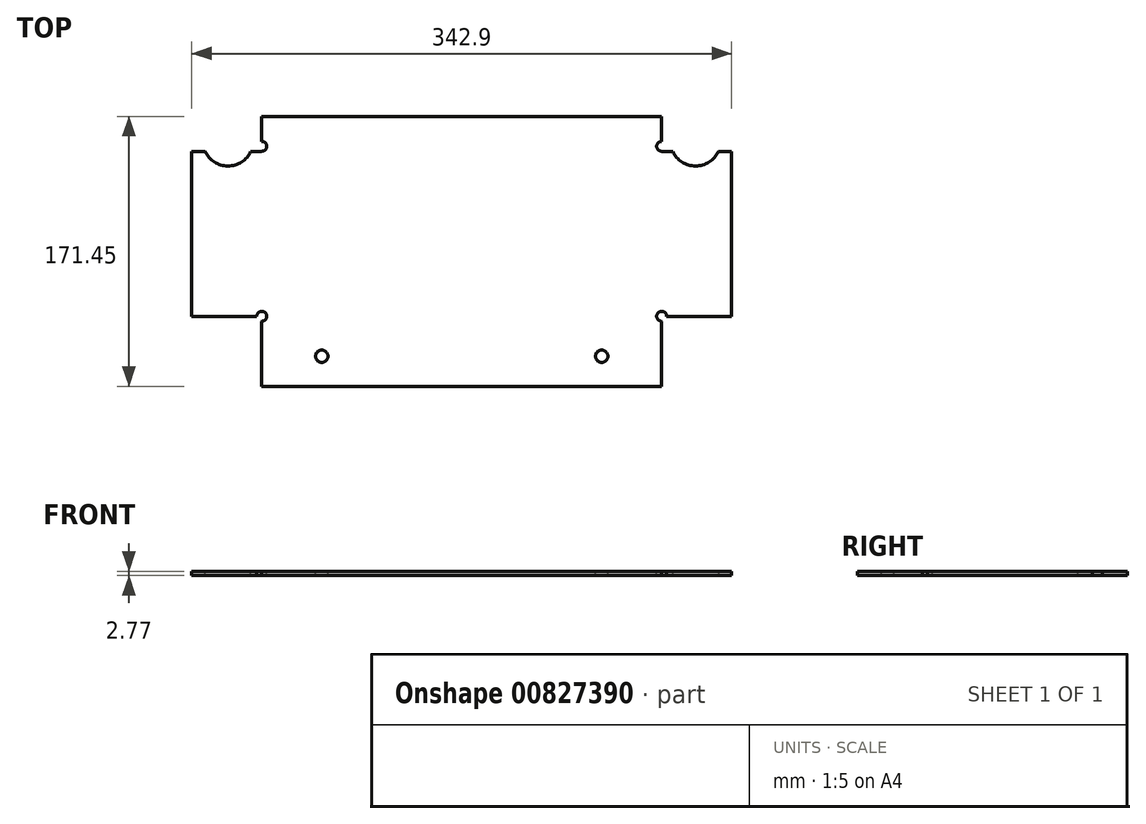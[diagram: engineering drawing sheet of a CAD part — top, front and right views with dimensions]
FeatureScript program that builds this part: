
annotation { "Feature Type Name" : "Feature", "Feature Type Description" : "" }
export const myFeature = defineFeature(function(context is Context, id is Id, definition is map)
    precondition{}
    {
        {
            var Q0;
            Q0=qCreatedBy(makeId("Top.planeOp"),FACE);
            var sketch = newSketch(context, id + "F0", { "sketchPlane" : qUnion([Q0])});
            skArc(sketch, "E0", {"start": v(-162.97, 39.69) * mm, "mid": v(-148.5, 30.35) * mm, "end": v(-134.04, 39.69) * mm});
            skLineSegment(sketch, "E1", {"start": v(-127, 61.91) * mm, "end": v(-127, 46.04) * mm});
            skLineSegment(sketch, "E2", {"start": v(-127, -68.26) * mm, "end": v(-127, -109.54) * mm});
            skLineSegment(sketch, "E3", {"start": v(130.18, -65.09) * mm, "end": v(171.45, -65.09) * mm});
            skLineSegment(sketch, "E4", {"start": v(127, -109.54) * mm, "end": v(-127, -109.54) * mm});
            skLineSegment(sketch, "E5", {"start": v(127, -68.26) * mm, "end": v(127, -109.54) * mm});
            skLineSegment(sketch, "E6", {"start": v(-127, 61.91) * mm, "end": v(127, 61.91) * mm});
            skLineSegment(sketch, "E7", {"start": v(127, 61.91) * mm, "end": v(127, 46.04) * mm});
            skArc(sketch, "E8", {"start": v(134.04, 39.69) * mm, "mid": v(148.5, 30.35) * mm, "end": v(162.97, 39.69) * mm});
            skArc(sketch, "E9", {"start": v(-127, 39.69) * mm, "mid": v(-123.83, 42.86) * mm, "end": v(-127, 46.04) * mm});
            skArc(sketch, "E10", {"start": v(127, 46.04) * mm, "mid": v(123.83, 42.86) * mm, "end": v(127, 39.69) * mm});
            skArc(sketch, "E11", {"start": v(130.18, -65.09) * mm, "mid": v(124.75, -62.84) * mm, "end": v(127, -68.26) * mm});
            skArc(sketch, "E12", {"start": v(-127, -68.26) * mm, "mid": v(-124.75, -62.84) * mm, "end": v(-130.18, -65.09) * mm});
            skLineSegment(sketch, "E13", {"start": v(-171.45, 39.69) * mm, "end": v(-162.97, 39.69) * mm});
            skLineSegment(sketch, "E14", {"start": v(162.97, 39.69) * mm, "end": v(171.45, 39.69) * mm});
            skLineSegment(sketch, "E15", {"start": v(-134.04, 39.69) * mm, "end": v(-127, 39.69) * mm});
            skLineSegment(sketch, "E16", {"start": v(127, 39.69) * mm, "end": v(134.04, 39.69) * mm});
            skCircle(sketch, "E17", {"center": v(-88.9, -90.49) * mm, "radius": 3.97 * mm});
            skCircle(sketch, "E18", {"center": v(88.9, -90.49) * mm, "radius": 3.97 * mm});
            skLineSegment(sketch, "E19", {"start": v(-171.45, 39.69) * mm, "end": v(-171.45, -65.09) * mm});
            skLineSegment(sketch, "E20", {"start": v(171.45, 39.69) * mm, "end": v(171.45, -65.09) * mm});
            skLineSegment(sketch, "E21", {"start": v(-130.18, -65.09) * mm, "end": v(-171.45, -65.09) * mm});
            skSolve(sketch);
        }
        {
            var Q0;
            Q0=sQuery(id+"F0.wireOp",EDGE,"E4");
            var Q1;
            Q1=sQuery(id+"F0.wireOp",EDGE,"E17");
            var Q2;
            Q2=sQuery(id+"F0.wireOp",EDGE,"E20");
            var Q3;
            Q3=sQuery(id+"F0.wireOp",EDGE,"E3");
            var Q4;
            Q4=sQuery(id+"F0.wireOp",EDGE,"E7");
            var Q5;
            Q5=sQuery(id+"F0.wireOp",EDGE,"E5");
            var Q6;
            Q6=sQuery(id+"F0.wireOp",EDGE,"E21");
            var Q7;
            Q7=sQuery(id+"F0.wireOp",EDGE,"E18");
            var Q8;
            Q8=sQuery(id+"F0.wireOp",EDGE,"E2");
            var Q9;
            Q9=sQuery(id+"F0.wireOp",EDGE,"E0");
            var Q10;
            Q10=sQuery(id+"F0.wireOp",EDGE,"E8");
            var Q11;
            Q11=sQuery(id+"F0.wireOp",EDGE,"E1");
            var Q12;
            Q12=sQuery(id+"F0.wireOp",EDGE,"E6");
            var Q13;
            Q13=sQuery(id+"F0.wireOp",EDGE,"E19");
            var Q14;
            Q14=sQuery(id+"F0.wireOp",EDGE,"E12");
            var Q15;
            Q15=sQuery(id+"F0.wireOp",EDGE,"E11");
            var Q16;
            Q16=sQuery(id+"F0.wireOp",EDGE,"E15");
            var Q17;
            Q17=sQuery(id+"F0.wireOp",EDGE,"E9");
            var Q18;
            Q18=sQuery(id+"F0.wireOp",EDGE,"E13");
            var Q19;
            Q19=sQuery(id+"F0.wireOp",EDGE,"E16");
            var Q20;
            Q20=sQuery(id+"F0.wireOp",EDGE,"E14");
            var Q21;
            Q21=sQuery(id+"F0.wireOp",EDGE,"E10");
            extrude(context, id + "F1", {"bodyType" : ToolBodyType.SURFACE, "surfaceEntities" : qUnion([Q0, Q1, Q2, Q3, Q4, Q5, Q6, Q7, Q8, Q9, Q10, Q11, Q12, Q13, Q14, Q15, Q16, Q17, Q18, Q19, Q20, Q21]), "depth" : 2.77 * mm, "offsetDistance" : 25.4 * mm});
        }
    });
